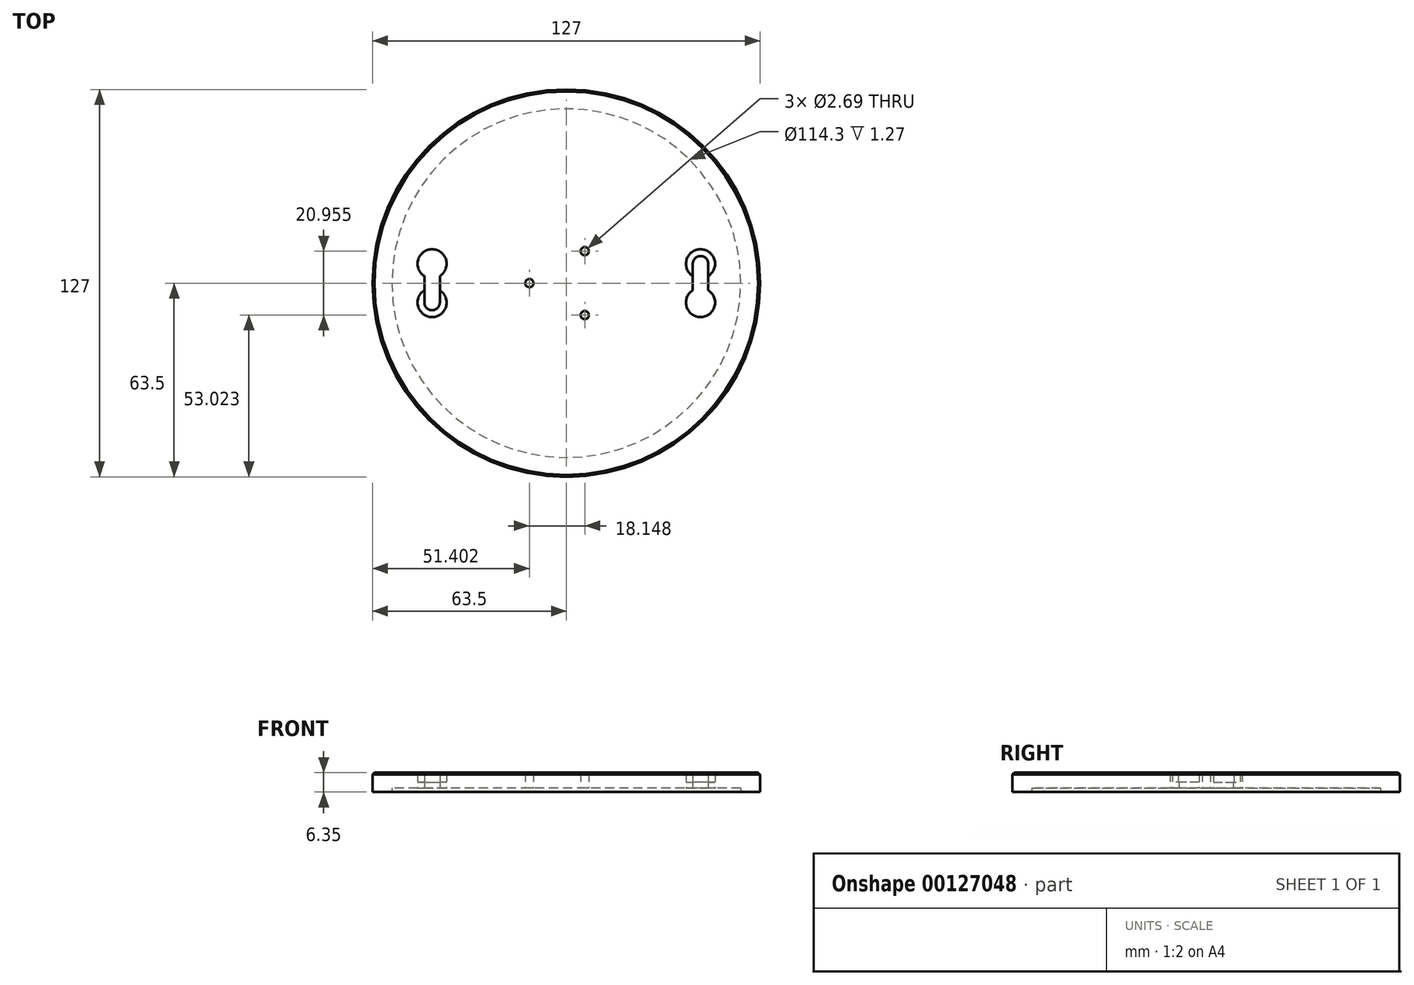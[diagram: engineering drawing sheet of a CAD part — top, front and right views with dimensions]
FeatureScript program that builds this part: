
annotation { "Feature Type Name" : "Feature", "Feature Type Description" : "" }
export const myFeature = defineFeature(function(context is Context, id is Id, definition is map)
    precondition{}
    {
        {
            var Q0;
            Q0=qCreatedBy(makeId("Top.planeOp"),FACE);
            var sketch = newSketch(context, id + "F0", { "sketchPlane" : qUnion([Q0])});
            skCircle(sketch, "E0", {"center": v(0, 0) * mm, "radius": 63.5 * mm});
            skCircle(sketch, "E1", {"center": v(0, 0) * mm, "radius": 44.45 * mm, "construction": true});
            skLineSegment(sketch, "E2", {"start": v(-63.5, 0) * mm, "end": v(63.5, 0) * mm, "construction": true});
            skLineSegment(sketch, "E3", {"start": v(0, -63.5) * mm, "end": v(0, 63.5) * mm, "construction": true});
            skCircle(sketch, "E4", {"center": v(-44, -6.35) * mm, "radius": 4.76 * mm});
            skCircle(sketch, "E5", {"center": v(-44, 6.35) * mm, "radius": 4.76 * mm});
            skCircle(sketch, "E6", {"center": v(-44, -6.35) * mm, "radius": 2.54 * mm});
            skLineSegment(sketch, "E7", {"start": v(-55.04, -6.35) * mm, "end": v(-32.06, -6.35) * mm, "construction": true});
            skLineSegment(sketch, "E8", {"start": v(-41.45, -6.35) * mm, "end": v(-41.45, 2.32) * mm});
            skLineSegment(sketch, "E9", {"start": v(-46.53, -6.35) * mm, "end": v(-46.53, 2.32) * mm});
            skCircle(sketch, "E10.cCircle", {"center": v(0, 0) * mm, "radius": 6.05 * mm, "construction": true});
            skLineSegment(sketch, "E10.0", {"start": v(6.05, 10.48) * mm, "end": v(6.05, -10.48) * mm, "construction": true});
            skLineSegment(sketch, "E10.1", {"start": v(6.05, -10.48) * mm, "end": v(-12.1, 0) * mm, "construction": true});
            skLineSegment(sketch, "E10.2", {"start": v(-12.1, 0) * mm, "end": v(6.05, 10.48) * mm, "construction": true});
            skPoint(sketch, "E10.0.midPoint", {"position": v(6.05, 0) * mm});
            skCircle(sketch, "E11", {"center": v(-12.1, 0) * mm, "radius": 1.35 * mm});
            skCircle(sketch, "E12.1.0", {"center": v(44, 6.35) * mm, "radius": 2.54 * mm});
            skLineSegment(sketch, "E12.1.1", {"start": v(41.45, 6.35) * mm, "end": v(41.45, -2.32) * mm});
            skCircle(sketch, "E12.1.2", {"center": v(44, -6.35) * mm, "radius": 4.76 * mm});
            skCircle(sketch, "E12.1.3", {"center": v(44, 6.35) * mm, "radius": 4.76 * mm});
            skLineSegment(sketch, "E12.1.4", {"start": v(55.04, 6.35) * mm, "end": v(32.06, 6.35) * mm, "construction": true});
            skLineSegment(sketch, "E12.1.5", {"start": v(46.53, 6.35) * mm, "end": v(46.53, -2.32) * mm});
            skCircle(sketch, "E13.1.0", {"center": v(6.05, -10.48) * mm, "radius": 1.35 * mm});
            skCircle(sketch, "E13.2.0", {"center": v(6.05, 10.48) * mm, "radius": 1.35 * mm});
            skCircle(sketch, "E14", {"center": v(0, 0) * mm, "radius": 57.15 * mm});
            skSolve(sketch);
        }
        {
            var Q0;
            Q0=makeQuery(id+"F0.imprint","IMPRINT",FACE,{"disambiguationData":[TD([[makeQuery(id+"F0.imprint","IMPRINT",EDGE,{"derivedFrom":sQuery(id+"F0.wireOp",EDGE,"E0")}),1.0]])]});
            var Q1;
            {var subQ0=sQuery(id+"F0.wireOp",EDGE,"E8");var subQ1=sQuery(id+"F0.wireOp",EDGE,"E4");var subQ2=makeQuery(id+"F0.imprint","INTERSECT",VERTEX,{"derivedFrom":[subQ1,subQ0]});Q1=makeQuery(id+"F0.imprint","IMPRINT",FACE,{"disambiguationData":[TD([[makeQuery(id+"F0.imprint","IMPRINT",EDGE,{"disambiguationData":[TD([[subQ2,1.0]])],"derivedFrom":subQ1}),1.0]])]});}
            var Q2;
            {var subQ0=sQuery(id+"F0.wireOp",EDGE,"E12.1.1");var subQ1=sQuery(id+"F0.wireOp",EDGE,"E12.1.0");var subQ2=makeQuery(id+"F0.imprint","INTERSECT",VERTEX,{"derivedFrom":[subQ1,subQ0]});Q2=makeQuery(id+"F0.imprint","IMPRINT",FACE,{"disambiguationData":[TD([[makeQuery(id+"F0.imprint","IMPRINT",EDGE,{"disambiguationData":[TD([[subQ2,1.0]])],"derivedFrom":subQ1}),-1.0]])]});}
            var Q3;
            Q3=makeQuery(id+"F0.imprint","IMPRINT",FACE,{"disambiguationData":[TD([[makeQuery(id+"F0.imprint","IMPRINT",EDGE,{"derivedFrom":sQuery(id+"F0.wireOp",EDGE,"E11")}),-1.0]])]});
            extrude(context, id + "F1", {"entities" : qUnion([Q0, Q1, Q2, Q3]), "depth" : 6.35 * mm});
        }
        {
            var Q0;
            {var subQ0=sQuery(id+"F0.wireOp",EDGE,"E8");var subQ1=sQuery(id+"F0.wireOp",EDGE,"E4");var subQ2=makeQuery(id+"F0.imprint","INTERSECT",VERTEX,{"derivedFrom":[subQ1,subQ0]});Q0=makeQuery(id+"F0.imprint","IMPRINT",FACE,{"disambiguationData":[TD([[makeQuery(id+"F0.imprint","IMPRINT",EDGE,{"disambiguationData":[TD([[subQ2,1.0]])],"derivedFrom":subQ1}),1.0]])]});}
            var Q1;
            {var subQ0=sQuery(id+"F0.wireOp",EDGE,"E8");var subQ1=sQuery(id+"F0.wireOp",EDGE,"E4");var subQ2=makeQuery(id+"F0.imprint","INTERSECT",VERTEX,{"derivedFrom":[subQ1,subQ0]});Q1=makeQuery(id+"F0.imprint","IMPRINT",FACE,{"disambiguationData":[TD([[makeQuery(id+"F0.imprint","IMPRINT",EDGE,{"disambiguationData":[TD([[subQ2,-1.0]])],"derivedFrom":subQ1}),1.0]])]});}
            var Q2;
            {var subQ0=sQuery(id+"F0.wireOp",EDGE,"E12.1.1");var subQ1=sQuery(id+"F0.wireOp",EDGE,"E12.1.0");var subQ2=makeQuery(id+"F0.imprint","INTERSECT",VERTEX,{"derivedFrom":[subQ1,subQ0]});Q2=makeQuery(id+"F0.imprint","IMPRINT",FACE,{"disambiguationData":[TD([[makeQuery(id+"F0.imprint","IMPRINT",EDGE,{"disambiguationData":[TD([[subQ2,-1.0]])],"derivedFrom":subQ1}),-1.0]])]});}
            var Q3;
            {var subQ0=sQuery(id+"F0.wireOp",EDGE,"E12.1.1");var subQ1=sQuery(id+"F0.wireOp",EDGE,"E12.1.0");var subQ2=makeQuery(id+"F0.imprint","INTERSECT",VERTEX,{"derivedFrom":[subQ1,subQ0]});Q3=makeQuery(id+"F0.imprint","IMPRINT",FACE,{"disambiguationData":[TD([[makeQuery(id+"F0.imprint","IMPRINT",EDGE,{"disambiguationData":[TD([[subQ2,1.0]])],"derivedFrom":subQ1}),-1.0]])]});}
            extrude(context, id + "F2", {"entities" : qUnion([Q0, Q1, Q2, Q3]), "operationType" : NewBodyOperationType.REMOVE, "endBound" : BoundingType.UP_TO_NEXT, "depth" : 25.4 * mm, "hasSecondDirection" : true, "secondDirectionOppositeDirection" : false, "secondDirectionDepth" : 3.17 * mm});
        }
        {
            var Q0;
            Q0=makeQuery(id+"F1.opExtrude","CAP_EDGE",EDGE,{"disambiguationData":[OSD([sQuery(id+"F0.wireOp",EDGE,"E0")])],"isStart":false});
            chamfer(context, id + "F3", {"entities" : qUnion([Q0]), "width" : 0.64 * mm, "tangentPropagation" : true});
        }
        {
            var Q0;
            Q0=makeQuery(id+"F0.imprint","IMPRINT",FACE,{"disambiguationData":[TD([[makeQuery(id+"F0.imprint","IMPRINT",EDGE,{"derivedFrom":sQuery(id+"F0.wireOp",EDGE,"E11")}),-1.0]])]});
            var Q1;
            {var subQ0=sQuery(id+"F0.wireOp",EDGE,"E8");var subQ1=sQuery(id+"F0.wireOp",EDGE,"E4");var subQ2=makeQuery(id+"F0.imprint","INTERSECT",VERTEX,{"derivedFrom":[subQ1,subQ0]});Q1=makeQuery(id+"F0.imprint","IMPRINT",FACE,{"disambiguationData":[TD([[makeQuery(id+"F0.imprint","IMPRINT",EDGE,{"disambiguationData":[TD([[subQ2,1.0]])],"derivedFrom":subQ1}),1.0]])]});}
            var Q2;
            {var subQ0=sQuery(id+"F0.wireOp",EDGE,"E12.1.1");var subQ1=sQuery(id+"F0.wireOp",EDGE,"E12.1.0");var subQ2=makeQuery(id+"F0.imprint","INTERSECT",VERTEX,{"derivedFrom":[subQ1,subQ0]});Q2=makeQuery(id+"F0.imprint","IMPRINT",FACE,{"disambiguationData":[TD([[makeQuery(id+"F0.imprint","IMPRINT",EDGE,{"disambiguationData":[TD([[subQ2,1.0]])],"derivedFrom":subQ1}),-1.0]])]});}
            extrude(context, id + "F4", {"entities" : qUnion([Q0, Q1, Q2]), "operationType" : NewBodyOperationType.REMOVE, "depth" : 1.27 * mm});
        }
    });
